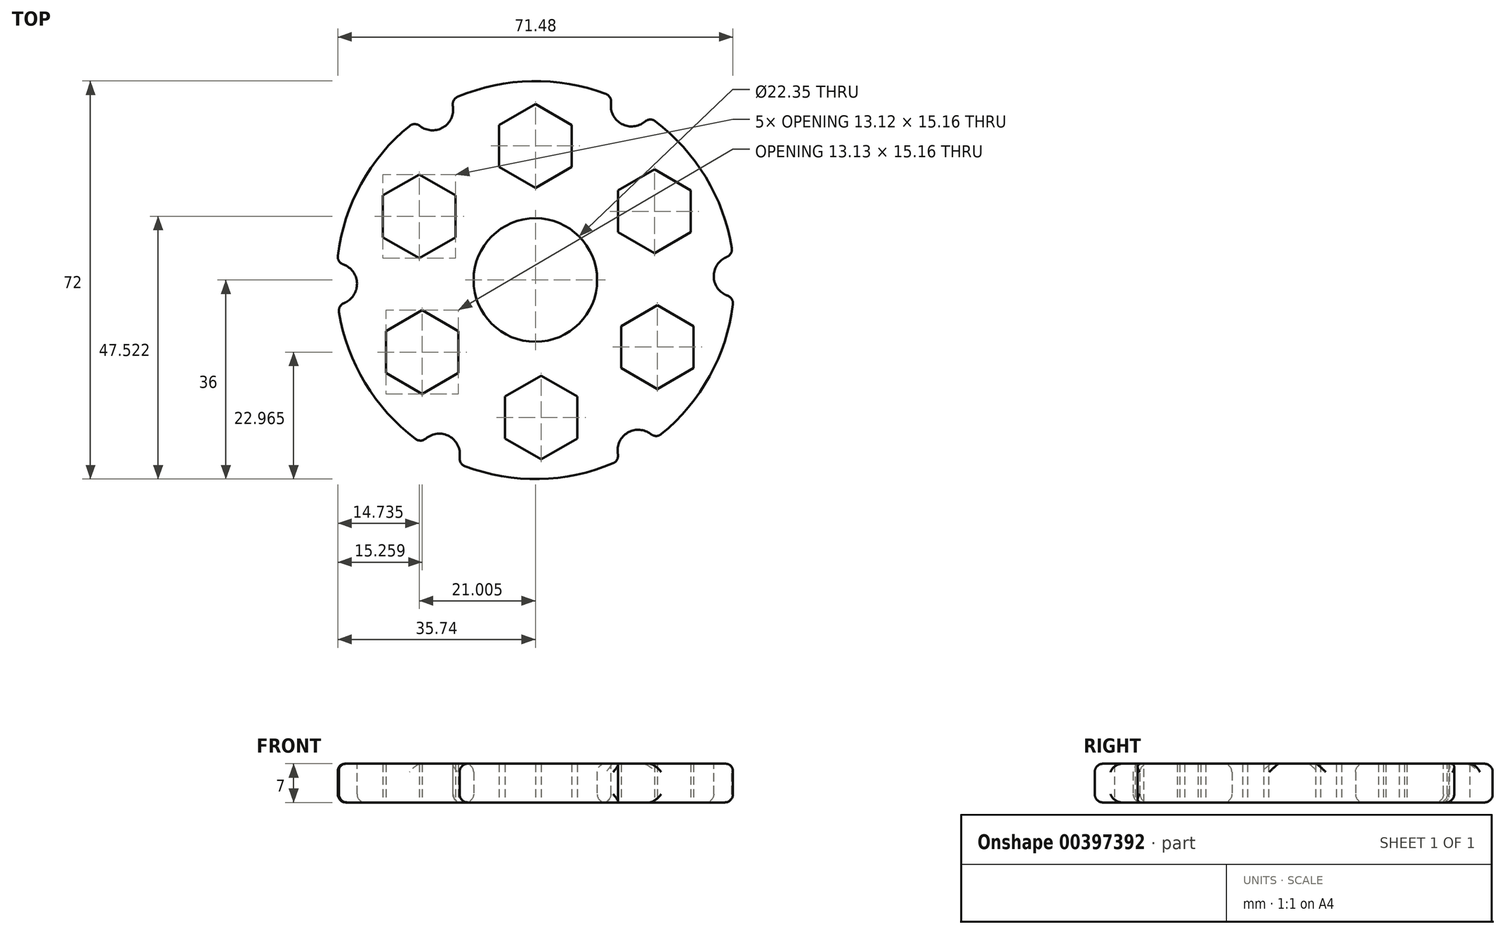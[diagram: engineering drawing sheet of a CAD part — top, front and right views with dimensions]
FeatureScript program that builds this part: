
annotation { "Feature Type Name" : "Feature", "Feature Type Description" : "" }
export const myFeature = defineFeature(function(context is Context, id is Id, definition is map)
    precondition{}
    {
        {
            var Q0;
            Q0=qCreatedBy(makeId("Top.planeOp"),FACE);
            var sketch = newSketch(context, id + "F0", { "sketchPlane" : qUnion([Q0])});
            skCircle(sketch, "E0", {"center": v(0, 0) * mm, "radius": 11.18 * mm});
            skCircle(sketch, "E1", {"center": v(0, 0) * mm, "radius": 36 * mm});
            skCircle(sketch, "E2.cCircle", {"center": v(0, 24.25) * mm, "radius": 6.56 * mm, "construction": true});
            skLineSegment(sketch, "E2.0", {"start": v(6.56, 28.04) * mm, "end": v(6.56, 20.47) * mm});
            skLineSegment(sketch, "E2.1", {"start": v(6.56, 20.47) * mm, "end": v(0, 16.68) * mm});
            skLineSegment(sketch, "E2.2", {"start": v(0, 16.68) * mm, "end": v(-6.56, 20.47) * mm});
            skLineSegment(sketch, "E2.3", {"start": v(-6.56, 20.47) * mm, "end": v(-6.56, 28.04) * mm});
            skLineSegment(sketch, "E2.4", {"start": v(-6.56, 28.04) * mm, "end": v(0, 31.83) * mm});
            skLineSegment(sketch, "E2.5", {"start": v(0, 31.83) * mm, "end": v(6.56, 28.04) * mm});
            skLineSegment(sketch, "E3.1.0", {"start": v(28.1, 8.64) * mm, "end": v(21.53, 4.85) * mm});
            skLineSegment(sketch, "E3.1.1", {"start": v(28.1, 16.22) * mm, "end": v(28.1, 8.64) * mm});
            skLineSegment(sketch, "E3.1.2", {"start": v(21.53, 20) * mm, "end": v(28.1, 16.22) * mm});
            skLineSegment(sketch, "E3.1.3", {"start": v(14.97, 16.22) * mm, "end": v(21.53, 20) * mm});
            skLineSegment(sketch, "E3.1.4", {"start": v(14.97, 8.64) * mm, "end": v(14.97, 16.22) * mm});
            skLineSegment(sketch, "E3.1.5", {"start": v(21.53, 4.85) * mm, "end": v(14.97, 8.64) * mm});
            skLineSegment(sketch, "E3.2.0", {"start": v(22.05, -19.7) * mm, "end": v(15.5, -15.92) * mm});
            skLineSegment(sketch, "E3.2.1", {"start": v(28.62, -15.92) * mm, "end": v(22.05, -19.7) * mm});
            skLineSegment(sketch, "E3.2.2", {"start": v(28.62, -8.34) * mm, "end": v(28.62, -15.92) * mm});
            skLineSegment(sketch, "E3.2.3", {"start": v(22.05, -4.55) * mm, "end": v(28.62, -8.34) * mm});
            skLineSegment(sketch, "E3.2.4", {"start": v(15.5, -8.34) * mm, "end": v(22.05, -4.55) * mm});
            skLineSegment(sketch, "E3.2.5", {"start": v(15.5, -15.92) * mm, "end": v(15.5, -8.34) * mm});
            skLineSegment(sketch, "E3.3.0", {"start": v(-5.51, -28.65) * mm, "end": v(-5.51, -21.07) * mm});
            skLineSegment(sketch, "E3.3.1", {"start": v(1.05, -32.44) * mm, "end": v(-5.51, -28.65) * mm});
            skLineSegment(sketch, "E3.3.2", {"start": v(7.61, -28.65) * mm, "end": v(1.05, -32.44) * mm});
            skLineSegment(sketch, "E3.3.3", {"start": v(7.61, -21.07) * mm, "end": v(7.61, -28.65) * mm});
            skLineSegment(sketch, "E3.3.4", {"start": v(1.05, -17.28) * mm, "end": v(7.61, -21.07) * mm});
            skLineSegment(sketch, "E3.3.5", {"start": v(-5.51, -21.07) * mm, "end": v(1.05, -17.28) * mm});
            skLineSegment(sketch, "E3.4.0", {"start": v(-27.04, -9.25) * mm, "end": v(-20.48, -5.46) * mm});
            skLineSegment(sketch, "E3.4.1", {"start": v(-27.04, -16.82) * mm, "end": v(-27.04, -9.25) * mm});
            skLineSegment(sketch, "E3.4.2", {"start": v(-20.48, -20.61) * mm, "end": v(-27.04, -16.82) * mm});
            skLineSegment(sketch, "E3.4.3", {"start": v(-13.92, -16.82) * mm, "end": v(-20.48, -20.61) * mm});
            skLineSegment(sketch, "E3.4.4", {"start": v(-13.92, -9.25) * mm, "end": v(-13.92, -16.82) * mm});
            skLineSegment(sketch, "E3.4.5", {"start": v(-20.48, -5.46) * mm, "end": v(-13.92, -9.25) * mm});
            skLineSegment(sketch, "E3.5.0", {"start": v(-21, 19.1) * mm, "end": v(-14.44, 15.31) * mm});
            skLineSegment(sketch, "E3.5.1", {"start": v(-27.57, 15.31) * mm, "end": v(-21, 19.1) * mm});
            skLineSegment(sketch, "E3.5.2", {"start": v(-27.57, 7.73) * mm, "end": v(-27.57, 15.31) * mm});
            skLineSegment(sketch, "E3.5.3", {"start": v(-21, 3.94) * mm, "end": v(-27.57, 7.73) * mm});
            skLineSegment(sketch, "E3.5.4", {"start": v(-14.44, 7.73) * mm, "end": v(-21, 3.94) * mm});
            skLineSegment(sketch, "E3.5.5", {"start": v(-14.44, 15.31) * mm, "end": v(-14.44, 7.73) * mm});
            skPoint(sketch, "E3.center", {"position": v(0.52, -0.3) * mm});
            skLineSegment(sketch, "E3.anchor1", {"start": v(0.52, -0.3) * mm, "end": v(6.56, 20.47) * mm, "construction": true});
            skLineSegment(sketch, "E3.anchor2", {"start": v(0.52, -0.3) * mm, "end": v(-14.44, 15.31) * mm, "construction": true});
            skSolve(sketch);
        }
        {
            var Q0;
            Q0=makeQuery(id+"F0.imprint","IMPRINT",FACE,{"disambiguationData":[TD([[makeQuery(id+"F0.imprint","IMPRINT",EDGE,{"derivedFrom":sQuery(id+"F0.wireOp",EDGE,"E0")}),-1.0]])]});
            extrude(context, id + "F1", {"entities" : qUnion([Q0]), "depth" : 7 * mm});
        }
        {
            var Q0;
            Q0=makeQuery(id+"F1.opExtrude","CAP_FACE",FACE,{"disambiguationData":[OSD([sQuery(id+"F0.wireOp",EDGE,"E0"),sQuery(id+"F0.wireOp",EDGE,"E1"),sQuery(id+"F0.wireOp",EDGE,"E2.0"),sQuery(id+"F0.wireOp",EDGE,"E2.1"),sQuery(id+"F0.wireOp",EDGE,"E2.2"),sQuery(id+"F0.wireOp",EDGE,"E2.3"),sQuery(id+"F0.wireOp",EDGE,"E2.4"),sQuery(id+"F0.wireOp",EDGE,"E2.5"),sQuery(id+"F0.wireOp",EDGE,"E3.1.0"),sQuery(id+"F0.wireOp",EDGE,"E3.1.1"),sQuery(id+"F0.wireOp",EDGE,"E3.1.2"),sQuery(id+"F0.wireOp",EDGE,"E3.1.3"),sQuery(id+"F0.wireOp",EDGE,"E3.1.4"),sQuery(id+"F0.wireOp",EDGE,"E3.1.5"),sQuery(id+"F0.wireOp",EDGE,"E3.2.0"),sQuery(id+"F0.wireOp",EDGE,"E3.2.1"),sQuery(id+"F0.wireOp",EDGE,"E3.2.2"),sQuery(id+"F0.wireOp",EDGE,"E3.2.3"),sQuery(id+"F0.wireOp",EDGE,"E3.2.4"),sQuery(id+"F0.wireOp",EDGE,"E3.2.5"),sQuery(id+"F0.wireOp",EDGE,"E3.3.0"),sQuery(id+"F0.wireOp",EDGE,"E3.3.1"),sQuery(id+"F0.wireOp",EDGE,"E3.3.2"),sQuery(id+"F0.wireOp",EDGE,"E3.3.3"),sQuery(id+"F0.wireOp",EDGE,"E3.3.4"),sQuery(id+"F0.wireOp",EDGE,"E3.3.5"),sQuery(id+"F0.wireOp",EDGE,"E3.4.0"),sQuery(id+"F0.wireOp",EDGE,"E3.4.1"),sQuery(id+"F0.wireOp",EDGE,"E3.4.2"),sQuery(id+"F0.wireOp",EDGE,"E3.4.3"),sQuery(id+"F0.wireOp",EDGE,"E3.4.4"),sQuery(id+"F0.wireOp",EDGE,"E3.4.5"),sQuery(id+"F0.wireOp",EDGE,"E3.5.0"),sQuery(id+"F0.wireOp",EDGE,"E3.5.1"),sQuery(id+"F0.wireOp",EDGE,"E3.5.2"),sQuery(id+"F0.wireOp",EDGE,"E3.5.3"),sQuery(id+"F0.wireOp",EDGE,"E3.5.4"),sQuery(id+"F0.wireOp",EDGE,"E3.5.5")])],"isStart":false});
            var sketch = newSketch(context, id + "F2", { "sketchPlane" : qUnion([Q0])});
            skCircle(sketch, "E4", {"center": v(17.4, 31.52) * mm, "radius": 3.73 * mm});
            skCircle(sketch, "E5.1.0", {"center": v(-18.6, 30.82) * mm, "radius": 3.73 * mm});
            skCircle(sketch, "E5.2.0", {"center": v(-36, -0.7) * mm, "radius": 3.73 * mm});
            skCircle(sketch, "E5.3.0", {"center": v(-17.4, -31.52) * mm, "radius": 3.73 * mm});
            skCircle(sketch, "E5.4.0", {"center": v(18.6, -30.82) * mm, "radius": 3.73 * mm});
            skCircle(sketch, "E5.5.0", {"center": v(36, 0.7) * mm, "radius": 3.73 * mm});
            skPoint(sketch, "E5.center", {"position": v(0, 0) * mm});
            skSolve(sketch);
        }
        {
            var Q0;
            {var subQ0=sQuery(id+"F2.wireOp",EDGE,"E5.1.0");var subQ1=makeQuery(id+"F1.opExtrude","CAP_EDGE",EDGE,{"disambiguationData":[OSD([sQuery(id+"F0.wireOp",EDGE,"E1")])],"isStart":false});var subQ2=makeQuery(id+"F2.imprint","INTERSECT",VERTEX,{"disambiguationData":[OD(0.0)],"derivedFrom":[subQ1,subQ0]});Q0=makeQuery(id+"F2.imprint","IMPRINT",FACE,{"disambiguationData":[TD([[makeQuery(id+"F2.imprint","IMPRINT",EDGE,{"disambiguationData":[TD([[subQ2,1.0]])],"derivedFrom":subQ0}),1.0]])]});}
            var Q1;
            {var subQ0=sQuery(id+"F2.wireOp",EDGE,"E5.1.0");var subQ1=makeQuery(id+"F1.opExtrude","CAP_EDGE",EDGE,{"disambiguationData":[OSD([sQuery(id+"F0.wireOp",EDGE,"E1")])],"isStart":false});var subQ2=makeQuery(id+"F2.imprint","INTERSECT",VERTEX,{"disambiguationData":[OD(0.0)],"derivedFrom":[subQ1,subQ0]});Q1=makeQuery(id+"F2.imprint","IMPRINT",FACE,{"disambiguationData":[TD([[makeQuery(id+"F2.imprint","IMPRINT",EDGE,{"disambiguationData":[TD([[subQ2,-1.0]])],"derivedFrom":subQ0}),1.0]])]});}
            var Q2;
            {var subQ0=sQuery(id+"F2.wireOp",EDGE,"E4");var subQ1=makeQuery(id+"F1.opExtrude","CAP_EDGE",EDGE,{"disambiguationData":[OSD([sQuery(id+"F0.wireOp",EDGE,"E1")])],"isStart":false});var subQ2=makeQuery(id+"F2.imprint","INTERSECT",VERTEX,{"disambiguationData":[OD(0.0)],"derivedFrom":[subQ1,subQ0]});Q2=makeQuery(id+"F2.imprint","IMPRINT",FACE,{"disambiguationData":[TD([[makeQuery(id+"F2.imprint","IMPRINT",EDGE,{"disambiguationData":[TD([[subQ2,1.0]])],"derivedFrom":subQ0}),1.0]])]});}
            var Q3;
            {var subQ0=sQuery(id+"F2.wireOp",EDGE,"E4");var subQ1=makeQuery(id+"F1.opExtrude","CAP_EDGE",EDGE,{"disambiguationData":[OSD([sQuery(id+"F0.wireOp",EDGE,"E1")])],"isStart":false});var subQ2=makeQuery(id+"F2.imprint","INTERSECT",VERTEX,{"disambiguationData":[OD(0.0)],"derivedFrom":[subQ1,subQ0]});Q3=makeQuery(id+"F2.imprint","IMPRINT",FACE,{"disambiguationData":[TD([[makeQuery(id+"F2.imprint","IMPRINT",EDGE,{"disambiguationData":[TD([[subQ2,-1.0]])],"derivedFrom":subQ0}),1.0]])]});}
            var Q4;
            {var subQ0=sQuery(id+"F2.wireOp",EDGE,"E5.5.0");var subQ1=makeQuery(id+"F1.opExtrude","CAP_EDGE",EDGE,{"disambiguationData":[OSD([sQuery(id+"F0.wireOp",EDGE,"E1")])],"isStart":false});var subQ2=makeQuery(id+"F2.imprint","INTERSECT",VERTEX,{"disambiguationData":[OD(0.0)],"derivedFrom":[subQ1,subQ0]});Q4=makeQuery(id+"F2.imprint","IMPRINT",FACE,{"disambiguationData":[TD([[makeQuery(id+"F2.imprint","IMPRINT",EDGE,{"disambiguationData":[TD([[subQ2,-1.0]])],"derivedFrom":subQ0}),1.0]])]});}
            var Q5;
            {var subQ0=sQuery(id+"F2.wireOp",EDGE,"E5.5.0");var subQ1=makeQuery(id+"F1.opExtrude","CAP_EDGE",EDGE,{"disambiguationData":[OSD([sQuery(id+"F0.wireOp",EDGE,"E1")])],"isStart":false});var subQ2=makeQuery(id+"F2.imprint","INTERSECT",VERTEX,{"disambiguationData":[OD(0.0)],"derivedFrom":[subQ1,subQ0]});Q5=makeQuery(id+"F2.imprint","IMPRINT",FACE,{"disambiguationData":[TD([[makeQuery(id+"F2.imprint","IMPRINT",EDGE,{"disambiguationData":[TD([[subQ2,1.0]])],"derivedFrom":subQ0}),1.0]])]});}
            var Q6;
            {var subQ0=sQuery(id+"F2.wireOp",EDGE,"E5.4.0");var subQ1=makeQuery(id+"F1.opExtrude","CAP_EDGE",EDGE,{"disambiguationData":[OSD([sQuery(id+"F0.wireOp",EDGE,"E1")])],"isStart":false});var subQ2=makeQuery(id+"F2.imprint","INTERSECT",VERTEX,{"disambiguationData":[OD(0.0)],"derivedFrom":[subQ1,subQ0]});Q6=makeQuery(id+"F2.imprint","IMPRINT",FACE,{"disambiguationData":[TD([[makeQuery(id+"F2.imprint","IMPRINT",EDGE,{"disambiguationData":[TD([[subQ2,-1.0]])],"derivedFrom":subQ0}),1.0]])]});}
            var Q7;
            {var subQ0=sQuery(id+"F2.wireOp",EDGE,"E5.4.0");var subQ1=makeQuery(id+"F1.opExtrude","CAP_EDGE",EDGE,{"disambiguationData":[OSD([sQuery(id+"F0.wireOp",EDGE,"E1")])],"isStart":false});var subQ2=makeQuery(id+"F2.imprint","INTERSECT",VERTEX,{"disambiguationData":[OD(0.0)],"derivedFrom":[subQ1,subQ0]});Q7=makeQuery(id+"F2.imprint","IMPRINT",FACE,{"disambiguationData":[TD([[makeQuery(id+"F2.imprint","IMPRINT",EDGE,{"disambiguationData":[TD([[subQ2,1.0]])],"derivedFrom":subQ0}),1.0]])]});}
            var Q8;
            {var subQ0=sQuery(id+"F2.wireOp",EDGE,"E5.3.0");var subQ1=makeQuery(id+"F1.opExtrude","CAP_EDGE",EDGE,{"disambiguationData":[OSD([sQuery(id+"F0.wireOp",EDGE,"E1")])],"isStart":false});var subQ2=makeQuery(id+"F2.imprint","INTERSECT",VERTEX,{"disambiguationData":[OD(0.0)],"derivedFrom":[subQ1,subQ0]});Q8=makeQuery(id+"F2.imprint","IMPRINT",FACE,{"disambiguationData":[TD([[makeQuery(id+"F2.imprint","IMPRINT",EDGE,{"disambiguationData":[TD([[subQ2,-1.0]])],"derivedFrom":subQ0}),1.0]])]});}
            var Q9;
            {var subQ0=sQuery(id+"F2.wireOp",EDGE,"E5.3.0");var subQ1=makeQuery(id+"F1.opExtrude","CAP_EDGE",EDGE,{"disambiguationData":[OSD([sQuery(id+"F0.wireOp",EDGE,"E1")])],"isStart":false});var subQ2=makeQuery(id+"F2.imprint","INTERSECT",VERTEX,{"disambiguationData":[OD(0.0)],"derivedFrom":[subQ1,subQ0]});Q9=makeQuery(id+"F2.imprint","IMPRINT",FACE,{"disambiguationData":[TD([[makeQuery(id+"F2.imprint","IMPRINT",EDGE,{"disambiguationData":[TD([[subQ2,1.0]])],"derivedFrom":subQ0}),1.0]])]});}
            var Q10;
            {var subQ0=sQuery(id+"F2.wireOp",EDGE,"E5.2.0");var subQ1=makeQuery(id+"F1.opExtrude","CAP_EDGE",EDGE,{"disambiguationData":[OSD([sQuery(id+"F0.wireOp",EDGE,"E1")])],"isStart":false});var subQ2=makeQuery(id+"F2.imprint","INTERSECT",VERTEX,{"disambiguationData":[OD(0.0)],"derivedFrom":[subQ1,subQ0]});Q10=makeQuery(id+"F2.imprint","IMPRINT",FACE,{"disambiguationData":[TD([[makeQuery(id+"F2.imprint","IMPRINT",EDGE,{"disambiguationData":[TD([[subQ2,1.0]])],"derivedFrom":subQ0}),1.0]])]});}
            var Q11;
            {var subQ0=sQuery(id+"F2.wireOp",EDGE,"E5.2.0");var subQ1=makeQuery(id+"F1.opExtrude","CAP_EDGE",EDGE,{"disambiguationData":[OSD([sQuery(id+"F0.wireOp",EDGE,"E1")])],"isStart":false});var subQ2=makeQuery(id+"F2.imprint","INTERSECT",VERTEX,{"disambiguationData":[OD(0.0)],"derivedFrom":[subQ1,subQ0]});Q11=makeQuery(id+"F2.imprint","IMPRINT",FACE,{"disambiguationData":[TD([[makeQuery(id+"F2.imprint","IMPRINT",EDGE,{"disambiguationData":[TD([[subQ2,-1.0]])],"derivedFrom":subQ0}),1.0]])]});}
            extrude(context, id + "F3", {"entities" : qUnion([Q0, Q1, Q2, Q3, Q4, Q5, Q6, Q7, Q8, Q9, Q10, Q11]), "operationType" : NewBodyOperationType.REMOVE, "oppositeDirection" : true, "depth" : 25 * mm});
        }
        {
            var Q0;
            {var subQ0=sQuery(id+"F0.wireOp",EDGE,"E1");Q0=makeQuery(id+"F3.boolean.opBoolean","SPLIT",EDGE,{"disambiguationData":[TD([makeQuery(id+"F1.opExtrude","CAP_FACE",FACE,{"disambiguationData":[OSD([sQuery(id+"F0.wireOp",EDGE,"E0"),subQ0,sQuery(id+"F0.wireOp",EDGE,"E2.0"),sQuery(id+"F0.wireOp",EDGE,"E2.1"),sQuery(id+"F0.wireOp",EDGE,"E2.2"),sQuery(id+"F0.wireOp",EDGE,"E2.3"),sQuery(id+"F0.wireOp",EDGE,"E2.4"),sQuery(id+"F0.wireOp",EDGE,"E2.5"),sQuery(id+"F0.wireOp",EDGE,"E3.1.0"),sQuery(id+"F0.wireOp",EDGE,"E3.1.1"),sQuery(id+"F0.wireOp",EDGE,"E3.1.2"),sQuery(id+"F0.wireOp",EDGE,"E3.1.3"),sQuery(id+"F0.wireOp",EDGE,"E3.1.4"),sQuery(id+"F0.wireOp",EDGE,"E3.1.5"),sQuery(id+"F0.wireOp",EDGE,"E3.2.0"),sQuery(id+"F0.wireOp",EDGE,"E3.2.1"),sQuery(id+"F0.wireOp",EDGE,"E3.2.2"),sQuery(id+"F0.wireOp",EDGE,"E3.2.3"),sQuery(id+"F0.wireOp",EDGE,"E3.2.4"),sQuery(id+"F0.wireOp",EDGE,"E3.2.5"),sQuery(id+"F0.wireOp",EDGE,"E3.3.0"),sQuery(id+"F0.wireOp",EDGE,"E3.3.1"),sQuery(id+"F0.wireOp",EDGE,"E3.3.2"),sQuery(id+"F0.wireOp",EDGE,"E3.3.3"),sQuery(id+"F0.wireOp",EDGE,"E3.3.4"),sQuery(id+"F0.wireOp",EDGE,"E3.3.5"),sQuery(id+"F0.wireOp",EDGE,"E3.4.0"),sQuery(id+"F0.wireOp",EDGE,"E3.4.1"),sQuery(id+"F0.wireOp",EDGE,"E3.4.2"),sQuery(id+"F0.wireOp",EDGE,"E3.4.3"),sQuery(id+"F0.wireOp",EDGE,"E3.4.4"),sQuery(id+"F0.wireOp",EDGE,"E3.4.5"),sQuery(id+"F0.wireOp",EDGE,"E3.5.0"),sQuery(id+"F0.wireOp",EDGE,"E3.5.1"),sQuery(id+"F0.wireOp",EDGE,"E3.5.2"),sQuery(id+"F0.wireOp",EDGE,"E3.5.3"),sQuery(id+"F0.wireOp",EDGE,"E3.5.4"),sQuery(id+"F0.wireOp",EDGE,"E3.5.5")])],"isStart":false}),makeQuery(id+"F1.opExtrude","SWEPT_FACE",FACE,{"disambiguationData":[OSD([subQ0])]}),makeQuery(id+"F3.opExtrude","SWEPT_FACE",FACE,{"disambiguationData":[OSD([sQuery(id+"F2.wireOp",EDGE,"E5.1.0")])]}),makeQuery(id+"F3.opExtrude","SWEPT_FACE",FACE,{"disambiguationData":[OSD([sQuery(id+"F2.wireOp",EDGE,"E5.2.0")])]})])],"derivedFrom":makeQuery(id+"F1.opExtrude","CAP_EDGE",EDGE,{"disambiguationData":[OSD([subQ0])],"isStart":false})});}
            var Q1;
            Q1=makeQuery(id+"F3.boolean.opBoolean","COPY",EDGE,{"derivedFrom":makeQuery(id+"F3.opExtrude","CAP_EDGE",EDGE,{"disambiguationData":[OSD([sQuery(id+"F2.wireOp",EDGE,"E5.1.0")])],"isStart":true})});
            var Q2;
            {var subQ0=sQuery(id+"F0.wireOp",EDGE,"E1");Q2=makeQuery(id+"F3.boolean.opBoolean","SPLIT",EDGE,{"disambiguationData":[TD([makeQuery(id+"F1.opExtrude","CAP_FACE",FACE,{"disambiguationData":[OSD([sQuery(id+"F0.wireOp",EDGE,"E0"),subQ0,sQuery(id+"F0.wireOp",EDGE,"E2.0"),sQuery(id+"F0.wireOp",EDGE,"E2.1"),sQuery(id+"F0.wireOp",EDGE,"E2.2"),sQuery(id+"F0.wireOp",EDGE,"E2.3"),sQuery(id+"F0.wireOp",EDGE,"E2.4"),sQuery(id+"F0.wireOp",EDGE,"E2.5"),sQuery(id+"F0.wireOp",EDGE,"E3.1.0"),sQuery(id+"F0.wireOp",EDGE,"E3.1.1"),sQuery(id+"F0.wireOp",EDGE,"E3.1.2"),sQuery(id+"F0.wireOp",EDGE,"E3.1.3"),sQuery(id+"F0.wireOp",EDGE,"E3.1.4"),sQuery(id+"F0.wireOp",EDGE,"E3.1.5"),sQuery(id+"F0.wireOp",EDGE,"E3.2.0"),sQuery(id+"F0.wireOp",EDGE,"E3.2.1"),sQuery(id+"F0.wireOp",EDGE,"E3.2.2"),sQuery(id+"F0.wireOp",EDGE,"E3.2.3"),sQuery(id+"F0.wireOp",EDGE,"E3.2.4"),sQuery(id+"F0.wireOp",EDGE,"E3.2.5"),sQuery(id+"F0.wireOp",EDGE,"E3.3.0"),sQuery(id+"F0.wireOp",EDGE,"E3.3.1"),sQuery(id+"F0.wireOp",EDGE,"E3.3.2"),sQuery(id+"F0.wireOp",EDGE,"E3.3.3"),sQuery(id+"F0.wireOp",EDGE,"E3.3.4"),sQuery(id+"F0.wireOp",EDGE,"E3.3.5"),sQuery(id+"F0.wireOp",EDGE,"E3.4.0"),sQuery(id+"F0.wireOp",EDGE,"E3.4.1"),sQuery(id+"F0.wireOp",EDGE,"E3.4.2"),sQuery(id+"F0.wireOp",EDGE,"E3.4.3"),sQuery(id+"F0.wireOp",EDGE,"E3.4.4"),sQuery(id+"F0.wireOp",EDGE,"E3.4.5"),sQuery(id+"F0.wireOp",EDGE,"E3.5.0"),sQuery(id+"F0.wireOp",EDGE,"E3.5.1"),sQuery(id+"F0.wireOp",EDGE,"E3.5.2"),sQuery(id+"F0.wireOp",EDGE,"E3.5.3"),sQuery(id+"F0.wireOp",EDGE,"E3.5.4"),sQuery(id+"F0.wireOp",EDGE,"E3.5.5")])],"isStart":false}),makeQuery(id+"F1.opExtrude","SWEPT_FACE",FACE,{"disambiguationData":[OSD([subQ0])]}),makeQuery(id+"F3.opExtrude","SWEPT_FACE",FACE,{"disambiguationData":[OSD([sQuery(id+"F2.wireOp",EDGE,"E4")])]}),makeQuery(id+"F3.opExtrude","SWEPT_FACE",FACE,{"disambiguationData":[OSD([sQuery(id+"F2.wireOp",EDGE,"E5.1.0")])]})])],"derivedFrom":makeQuery(id+"F1.opExtrude","CAP_EDGE",EDGE,{"disambiguationData":[OSD([subQ0])],"isStart":false})});}
            var Q3;
            Q3=makeQuery(id+"F3.boolean.opBoolean","COPY",EDGE,{"derivedFrom":makeQuery(id+"F3.opExtrude","CAP_EDGE",EDGE,{"disambiguationData":[OSD([sQuery(id+"F2.wireOp",EDGE,"E4")])],"isStart":true})});
            var Q4;
            {var subQ0=sQuery(id+"F0.wireOp",EDGE,"E1");Q4=makeQuery(id+"F3.boolean.opBoolean","SPLIT",EDGE,{"disambiguationData":[TD([makeQuery(id+"F1.opExtrude","CAP_FACE",FACE,{"disambiguationData":[OSD([sQuery(id+"F0.wireOp",EDGE,"E0"),subQ0,sQuery(id+"F0.wireOp",EDGE,"E2.0"),sQuery(id+"F0.wireOp",EDGE,"E2.1"),sQuery(id+"F0.wireOp",EDGE,"E2.2"),sQuery(id+"F0.wireOp",EDGE,"E2.3"),sQuery(id+"F0.wireOp",EDGE,"E2.4"),sQuery(id+"F0.wireOp",EDGE,"E2.5"),sQuery(id+"F0.wireOp",EDGE,"E3.1.0"),sQuery(id+"F0.wireOp",EDGE,"E3.1.1"),sQuery(id+"F0.wireOp",EDGE,"E3.1.2"),sQuery(id+"F0.wireOp",EDGE,"E3.1.3"),sQuery(id+"F0.wireOp",EDGE,"E3.1.4"),sQuery(id+"F0.wireOp",EDGE,"E3.1.5"),sQuery(id+"F0.wireOp",EDGE,"E3.2.0"),sQuery(id+"F0.wireOp",EDGE,"E3.2.1"),sQuery(id+"F0.wireOp",EDGE,"E3.2.2"),sQuery(id+"F0.wireOp",EDGE,"E3.2.3"),sQuery(id+"F0.wireOp",EDGE,"E3.2.4"),sQuery(id+"F0.wireOp",EDGE,"E3.2.5"),sQuery(id+"F0.wireOp",EDGE,"E3.3.0"),sQuery(id+"F0.wireOp",EDGE,"E3.3.1"),sQuery(id+"F0.wireOp",EDGE,"E3.3.2"),sQuery(id+"F0.wireOp",EDGE,"E3.3.3"),sQuery(id+"F0.wireOp",EDGE,"E3.3.4"),sQuery(id+"F0.wireOp",EDGE,"E3.3.5"),sQuery(id+"F0.wireOp",EDGE,"E3.4.0"),sQuery(id+"F0.wireOp",EDGE,"E3.4.1"),sQuery(id+"F0.wireOp",EDGE,"E3.4.2"),sQuery(id+"F0.wireOp",EDGE,"E3.4.3"),sQuery(id+"F0.wireOp",EDGE,"E3.4.4"),sQuery(id+"F0.wireOp",EDGE,"E3.4.5"),sQuery(id+"F0.wireOp",EDGE,"E3.5.0"),sQuery(id+"F0.wireOp",EDGE,"E3.5.1"),sQuery(id+"F0.wireOp",EDGE,"E3.5.2"),sQuery(id+"F0.wireOp",EDGE,"E3.5.3"),sQuery(id+"F0.wireOp",EDGE,"E3.5.4"),sQuery(id+"F0.wireOp",EDGE,"E3.5.5")])],"isStart":false}),makeQuery(id+"F1.opExtrude","SWEPT_FACE",FACE,{"disambiguationData":[OSD([subQ0])]}),makeQuery(id+"F3.opExtrude","SWEPT_FACE",FACE,{"disambiguationData":[OSD([sQuery(id+"F2.wireOp",EDGE,"E4")])]}),makeQuery(id+"F3.opExtrude","SWEPT_FACE",FACE,{"disambiguationData":[OSD([sQuery(id+"F2.wireOp",EDGE,"E5.5.0")])]})])],"derivedFrom":makeQuery(id+"F1.opExtrude","CAP_EDGE",EDGE,{"disambiguationData":[OSD([subQ0])],"isStart":false})});}
            var Q5;
            Q5=makeQuery(id+"F3.boolean.opBoolean","COPY",EDGE,{"derivedFrom":makeQuery(id+"F3.opExtrude","CAP_EDGE",EDGE,{"disambiguationData":[OSD([sQuery(id+"F2.wireOp",EDGE,"E5.5.0")])],"isStart":true})});
            var Q6;
            {var subQ0=sQuery(id+"F0.wireOp",EDGE,"E1");Q6=makeQuery(id+"F3.boolean.opBoolean","SPLIT",EDGE,{"disambiguationData":[TD([makeQuery(id+"F1.opExtrude","CAP_FACE",FACE,{"disambiguationData":[OSD([sQuery(id+"F0.wireOp",EDGE,"E0"),subQ0,sQuery(id+"F0.wireOp",EDGE,"E2.0"),sQuery(id+"F0.wireOp",EDGE,"E2.1"),sQuery(id+"F0.wireOp",EDGE,"E2.2"),sQuery(id+"F0.wireOp",EDGE,"E2.3"),sQuery(id+"F0.wireOp",EDGE,"E2.4"),sQuery(id+"F0.wireOp",EDGE,"E2.5"),sQuery(id+"F0.wireOp",EDGE,"E3.1.0"),sQuery(id+"F0.wireOp",EDGE,"E3.1.1"),sQuery(id+"F0.wireOp",EDGE,"E3.1.2"),sQuery(id+"F0.wireOp",EDGE,"E3.1.3"),sQuery(id+"F0.wireOp",EDGE,"E3.1.4"),sQuery(id+"F0.wireOp",EDGE,"E3.1.5"),sQuery(id+"F0.wireOp",EDGE,"E3.2.0"),sQuery(id+"F0.wireOp",EDGE,"E3.2.1"),sQuery(id+"F0.wireOp",EDGE,"E3.2.2"),sQuery(id+"F0.wireOp",EDGE,"E3.2.3"),sQuery(id+"F0.wireOp",EDGE,"E3.2.4"),sQuery(id+"F0.wireOp",EDGE,"E3.2.5"),sQuery(id+"F0.wireOp",EDGE,"E3.3.0"),sQuery(id+"F0.wireOp",EDGE,"E3.3.1"),sQuery(id+"F0.wireOp",EDGE,"E3.3.2"),sQuery(id+"F0.wireOp",EDGE,"E3.3.3"),sQuery(id+"F0.wireOp",EDGE,"E3.3.4"),sQuery(id+"F0.wireOp",EDGE,"E3.3.5"),sQuery(id+"F0.wireOp",EDGE,"E3.4.0"),sQuery(id+"F0.wireOp",EDGE,"E3.4.1"),sQuery(id+"F0.wireOp",EDGE,"E3.4.2"),sQuery(id+"F0.wireOp",EDGE,"E3.4.3"),sQuery(id+"F0.wireOp",EDGE,"E3.4.4"),sQuery(id+"F0.wireOp",EDGE,"E3.4.5"),sQuery(id+"F0.wireOp",EDGE,"E3.5.0"),sQuery(id+"F0.wireOp",EDGE,"E3.5.1"),sQuery(id+"F0.wireOp",EDGE,"E3.5.2"),sQuery(id+"F0.wireOp",EDGE,"E3.5.3"),sQuery(id+"F0.wireOp",EDGE,"E3.5.4"),sQuery(id+"F0.wireOp",EDGE,"E3.5.5")])],"isStart":false}),makeQuery(id+"F1.opExtrude","SWEPT_FACE",FACE,{"disambiguationData":[OSD([subQ0])]}),makeQuery(id+"F3.opExtrude","SWEPT_FACE",FACE,{"disambiguationData":[OSD([sQuery(id+"F2.wireOp",EDGE,"E5.4.0")])]}),makeQuery(id+"F3.opExtrude","SWEPT_FACE",FACE,{"disambiguationData":[OSD([sQuery(id+"F2.wireOp",EDGE,"E5.5.0")])]})])],"derivedFrom":makeQuery(id+"F1.opExtrude","CAP_EDGE",EDGE,{"disambiguationData":[OSD([subQ0])],"isStart":false})});}
            var Q7;
            Q7=makeQuery(id+"F3.boolean.opBoolean","COPY",EDGE,{"derivedFrom":makeQuery(id+"F3.opExtrude","CAP_EDGE",EDGE,{"disambiguationData":[OSD([sQuery(id+"F2.wireOp",EDGE,"E5.4.0")])],"isStart":true})});
            var Q8;
            {var subQ0=sQuery(id+"F0.wireOp",EDGE,"E1");Q8=makeQuery(id+"F3.boolean.opBoolean","SPLIT",EDGE,{"disambiguationData":[TD([makeQuery(id+"F1.opExtrude","CAP_FACE",FACE,{"disambiguationData":[OSD([sQuery(id+"F0.wireOp",EDGE,"E0"),subQ0,sQuery(id+"F0.wireOp",EDGE,"E2.0"),sQuery(id+"F0.wireOp",EDGE,"E2.1"),sQuery(id+"F0.wireOp",EDGE,"E2.2"),sQuery(id+"F0.wireOp",EDGE,"E2.3"),sQuery(id+"F0.wireOp",EDGE,"E2.4"),sQuery(id+"F0.wireOp",EDGE,"E2.5"),sQuery(id+"F0.wireOp",EDGE,"E3.1.0"),sQuery(id+"F0.wireOp",EDGE,"E3.1.1"),sQuery(id+"F0.wireOp",EDGE,"E3.1.2"),sQuery(id+"F0.wireOp",EDGE,"E3.1.3"),sQuery(id+"F0.wireOp",EDGE,"E3.1.4"),sQuery(id+"F0.wireOp",EDGE,"E3.1.5"),sQuery(id+"F0.wireOp",EDGE,"E3.2.0"),sQuery(id+"F0.wireOp",EDGE,"E3.2.1"),sQuery(id+"F0.wireOp",EDGE,"E3.2.2"),sQuery(id+"F0.wireOp",EDGE,"E3.2.3"),sQuery(id+"F0.wireOp",EDGE,"E3.2.4"),sQuery(id+"F0.wireOp",EDGE,"E3.2.5"),sQuery(id+"F0.wireOp",EDGE,"E3.3.0"),sQuery(id+"F0.wireOp",EDGE,"E3.3.1"),sQuery(id+"F0.wireOp",EDGE,"E3.3.2"),sQuery(id+"F0.wireOp",EDGE,"E3.3.3"),sQuery(id+"F0.wireOp",EDGE,"E3.3.4"),sQuery(id+"F0.wireOp",EDGE,"E3.3.5"),sQuery(id+"F0.wireOp",EDGE,"E3.4.0"),sQuery(id+"F0.wireOp",EDGE,"E3.4.1"),sQuery(id+"F0.wireOp",EDGE,"E3.4.2"),sQuery(id+"F0.wireOp",EDGE,"E3.4.3"),sQuery(id+"F0.wireOp",EDGE,"E3.4.4"),sQuery(id+"F0.wireOp",EDGE,"E3.4.5"),sQuery(id+"F0.wireOp",EDGE,"E3.5.0"),sQuery(id+"F0.wireOp",EDGE,"E3.5.1"),sQuery(id+"F0.wireOp",EDGE,"E3.5.2"),sQuery(id+"F0.wireOp",EDGE,"E3.5.3"),sQuery(id+"F0.wireOp",EDGE,"E3.5.4"),sQuery(id+"F0.wireOp",EDGE,"E3.5.5")])],"isStart":false}),makeQuery(id+"F1.opExtrude","SWEPT_FACE",FACE,{"disambiguationData":[OSD([subQ0])]}),makeQuery(id+"F3.opExtrude","SWEPT_FACE",FACE,{"disambiguationData":[OSD([sQuery(id+"F2.wireOp",EDGE,"E5.3.0")])]}),makeQuery(id+"F3.opExtrude","SWEPT_FACE",FACE,{"disambiguationData":[OSD([sQuery(id+"F2.wireOp",EDGE,"E5.4.0")])]})])],"derivedFrom":makeQuery(id+"F1.opExtrude","CAP_EDGE",EDGE,{"disambiguationData":[OSD([subQ0])],"isStart":false})});}
            var Q9;
            Q9=makeQuery(id+"F3.boolean.opBoolean","COPY",EDGE,{"derivedFrom":makeQuery(id+"F3.opExtrude","CAP_EDGE",EDGE,{"disambiguationData":[OSD([sQuery(id+"F2.wireOp",EDGE,"E5.3.0")])],"isStart":true})});
            var Q10;
            {var subQ0=sQuery(id+"F0.wireOp",EDGE,"E1");Q10=makeQuery(id+"F3.boolean.opBoolean","SPLIT",EDGE,{"disambiguationData":[TD([makeQuery(id+"F1.opExtrude","CAP_FACE",FACE,{"disambiguationData":[OSD([sQuery(id+"F0.wireOp",EDGE,"E0"),subQ0,sQuery(id+"F0.wireOp",EDGE,"E2.0"),sQuery(id+"F0.wireOp",EDGE,"E2.1"),sQuery(id+"F0.wireOp",EDGE,"E2.2"),sQuery(id+"F0.wireOp",EDGE,"E2.3"),sQuery(id+"F0.wireOp",EDGE,"E2.4"),sQuery(id+"F0.wireOp",EDGE,"E2.5"),sQuery(id+"F0.wireOp",EDGE,"E3.1.0"),sQuery(id+"F0.wireOp",EDGE,"E3.1.1"),sQuery(id+"F0.wireOp",EDGE,"E3.1.2"),sQuery(id+"F0.wireOp",EDGE,"E3.1.3"),sQuery(id+"F0.wireOp",EDGE,"E3.1.4"),sQuery(id+"F0.wireOp",EDGE,"E3.1.5"),sQuery(id+"F0.wireOp",EDGE,"E3.2.0"),sQuery(id+"F0.wireOp",EDGE,"E3.2.1"),sQuery(id+"F0.wireOp",EDGE,"E3.2.2"),sQuery(id+"F0.wireOp",EDGE,"E3.2.3"),sQuery(id+"F0.wireOp",EDGE,"E3.2.4"),sQuery(id+"F0.wireOp",EDGE,"E3.2.5"),sQuery(id+"F0.wireOp",EDGE,"E3.3.0"),sQuery(id+"F0.wireOp",EDGE,"E3.3.1"),sQuery(id+"F0.wireOp",EDGE,"E3.3.2"),sQuery(id+"F0.wireOp",EDGE,"E3.3.3"),sQuery(id+"F0.wireOp",EDGE,"E3.3.4"),sQuery(id+"F0.wireOp",EDGE,"E3.3.5"),sQuery(id+"F0.wireOp",EDGE,"E3.4.0"),sQuery(id+"F0.wireOp",EDGE,"E3.4.1"),sQuery(id+"F0.wireOp",EDGE,"E3.4.2"),sQuery(id+"F0.wireOp",EDGE,"E3.4.3"),sQuery(id+"F0.wireOp",EDGE,"E3.4.4"),sQuery(id+"F0.wireOp",EDGE,"E3.4.5"),sQuery(id+"F0.wireOp",EDGE,"E3.5.0"),sQuery(id+"F0.wireOp",EDGE,"E3.5.1"),sQuery(id+"F0.wireOp",EDGE,"E3.5.2"),sQuery(id+"F0.wireOp",EDGE,"E3.5.3"),sQuery(id+"F0.wireOp",EDGE,"E3.5.4"),sQuery(id+"F0.wireOp",EDGE,"E3.5.5")])],"isStart":false}),makeQuery(id+"F1.opExtrude","SWEPT_FACE",FACE,{"disambiguationData":[OSD([subQ0])]}),makeQuery(id+"F3.opExtrude","SWEPT_FACE",FACE,{"disambiguationData":[OSD([sQuery(id+"F2.wireOp",EDGE,"E5.2.0")])]}),makeQuery(id+"F3.opExtrude","SWEPT_FACE",FACE,{"disambiguationData":[OSD([sQuery(id+"F2.wireOp",EDGE,"E5.3.0")])]})])],"derivedFrom":makeQuery(id+"F1.opExtrude","CAP_EDGE",EDGE,{"disambiguationData":[OSD([subQ0])],"isStart":false})});}
            var Q11;
            Q11=makeQuery(id+"F3.boolean.opBoolean","COPY",EDGE,{"derivedFrom":makeQuery(id+"F3.opExtrude","CAP_EDGE",EDGE,{"disambiguationData":[OSD([sQuery(id+"F2.wireOp",EDGE,"E5.2.0")])],"isStart":true})});
            var Q12;
            {var subQ0=sQuery(id+"F0.wireOp",EDGE,"E1");Q12=makeQuery(id+"F3.boolean.opBoolean","SPLIT",EDGE,{"disambiguationData":[TD([makeQuery(id+"F1.opExtrude","CAP_FACE",FACE,{"disambiguationData":[OSD([sQuery(id+"F0.wireOp",EDGE,"E0"),subQ0,sQuery(id+"F0.wireOp",EDGE,"E2.0"),sQuery(id+"F0.wireOp",EDGE,"E2.1"),sQuery(id+"F0.wireOp",EDGE,"E2.2"),sQuery(id+"F0.wireOp",EDGE,"E2.3"),sQuery(id+"F0.wireOp",EDGE,"E2.4"),sQuery(id+"F0.wireOp",EDGE,"E2.5"),sQuery(id+"F0.wireOp",EDGE,"E3.1.0"),sQuery(id+"F0.wireOp",EDGE,"E3.1.1"),sQuery(id+"F0.wireOp",EDGE,"E3.1.2"),sQuery(id+"F0.wireOp",EDGE,"E3.1.3"),sQuery(id+"F0.wireOp",EDGE,"E3.1.4"),sQuery(id+"F0.wireOp",EDGE,"E3.1.5"),sQuery(id+"F0.wireOp",EDGE,"E3.2.0"),sQuery(id+"F0.wireOp",EDGE,"E3.2.1"),sQuery(id+"F0.wireOp",EDGE,"E3.2.2"),sQuery(id+"F0.wireOp",EDGE,"E3.2.3"),sQuery(id+"F0.wireOp",EDGE,"E3.2.4"),sQuery(id+"F0.wireOp",EDGE,"E3.2.5"),sQuery(id+"F0.wireOp",EDGE,"E3.3.0"),sQuery(id+"F0.wireOp",EDGE,"E3.3.1"),sQuery(id+"F0.wireOp",EDGE,"E3.3.2"),sQuery(id+"F0.wireOp",EDGE,"E3.3.3"),sQuery(id+"F0.wireOp",EDGE,"E3.3.4"),sQuery(id+"F0.wireOp",EDGE,"E3.3.5"),sQuery(id+"F0.wireOp",EDGE,"E3.4.0"),sQuery(id+"F0.wireOp",EDGE,"E3.4.1"),sQuery(id+"F0.wireOp",EDGE,"E3.4.2"),sQuery(id+"F0.wireOp",EDGE,"E3.4.3"),sQuery(id+"F0.wireOp",EDGE,"E3.4.4"),sQuery(id+"F0.wireOp",EDGE,"E3.4.5"),sQuery(id+"F0.wireOp",EDGE,"E3.5.0"),sQuery(id+"F0.wireOp",EDGE,"E3.5.1"),sQuery(id+"F0.wireOp",EDGE,"E3.5.2"),sQuery(id+"F0.wireOp",EDGE,"E3.5.3"),sQuery(id+"F0.wireOp",EDGE,"E3.5.4"),sQuery(id+"F0.wireOp",EDGE,"E3.5.5")])],"isStart":true}),makeQuery(id+"F1.opExtrude","SWEPT_FACE",FACE,{"disambiguationData":[OSD([subQ0])]}),makeQuery(id+"F3.opExtrude","SWEPT_FACE",FACE,{"disambiguationData":[OSD([sQuery(id+"F2.wireOp",EDGE,"E5.4.0")])]}),makeQuery(id+"F3.opExtrude","SWEPT_FACE",FACE,{"disambiguationData":[OSD([sQuery(id+"F2.wireOp",EDGE,"E5.5.0")])]})])],"derivedFrom":makeQuery(id+"F1.opExtrude","CAP_EDGE",EDGE,{"disambiguationData":[OSD([subQ0])],"isStart":true})});}
            var Q13;
            Q13=makeQuery(id+"F3.boolean.opBoolean","INTERSECT",EDGE,{"derivedFrom":[makeQuery(id+"F1.opExtrude","CAP_FACE",FACE,{"disambiguationData":[OSD([sQuery(id+"F0.wireOp",EDGE,"E0"),sQuery(id+"F0.wireOp",EDGE,"E1"),sQuery(id+"F0.wireOp",EDGE,"E2.0"),sQuery(id+"F0.wireOp",EDGE,"E2.1"),sQuery(id+"F0.wireOp",EDGE,"E2.2"),sQuery(id+"F0.wireOp",EDGE,"E2.3"),sQuery(id+"F0.wireOp",EDGE,"E2.4"),sQuery(id+"F0.wireOp",EDGE,"E2.5"),sQuery(id+"F0.wireOp",EDGE,"E3.1.0"),sQuery(id+"F0.wireOp",EDGE,"E3.1.1"),sQuery(id+"F0.wireOp",EDGE,"E3.1.2"),sQuery(id+"F0.wireOp",EDGE,"E3.1.3"),sQuery(id+"F0.wireOp",EDGE,"E3.1.4"),sQuery(id+"F0.wireOp",EDGE,"E3.1.5"),sQuery(id+"F0.wireOp",EDGE,"E3.2.0"),sQuery(id+"F0.wireOp",EDGE,"E3.2.1"),sQuery(id+"F0.wireOp",EDGE,"E3.2.2"),sQuery(id+"F0.wireOp",EDGE,"E3.2.3"),sQuery(id+"F0.wireOp",EDGE,"E3.2.4"),sQuery(id+"F0.wireOp",EDGE,"E3.2.5"),sQuery(id+"F0.wireOp",EDGE,"E3.3.0"),sQuery(id+"F0.wireOp",EDGE,"E3.3.1"),sQuery(id+"F0.wireOp",EDGE,"E3.3.2"),sQuery(id+"F0.wireOp",EDGE,"E3.3.3"),sQuery(id+"F0.wireOp",EDGE,"E3.3.4"),sQuery(id+"F0.wireOp",EDGE,"E3.3.5"),sQuery(id+"F0.wireOp",EDGE,"E3.4.0"),sQuery(id+"F0.wireOp",EDGE,"E3.4.1"),sQuery(id+"F0.wireOp",EDGE,"E3.4.2"),sQuery(id+"F0.wireOp",EDGE,"E3.4.3"),sQuery(id+"F0.wireOp",EDGE,"E3.4.4"),sQuery(id+"F0.wireOp",EDGE,"E3.4.5"),sQuery(id+"F0.wireOp",EDGE,"E3.5.0"),sQuery(id+"F0.wireOp",EDGE,"E3.5.1"),sQuery(id+"F0.wireOp",EDGE,"E3.5.2"),sQuery(id+"F0.wireOp",EDGE,"E3.5.3"),sQuery(id+"F0.wireOp",EDGE,"E3.5.4"),sQuery(id+"F0.wireOp",EDGE,"E3.5.5")])],"isStart":true}),makeQuery(id+"F3.opExtrude","SWEPT_FACE",FACE,{"disambiguationData":[OSD([sQuery(id+"F2.wireOp",EDGE,"E5.5.0")])]})]});
            var Q14;
            {var subQ0=sQuery(id+"F0.wireOp",EDGE,"E1");Q14=makeQuery(id+"F3.boolean.opBoolean","SPLIT",EDGE,{"disambiguationData":[TD([makeQuery(id+"F1.opExtrude","CAP_FACE",FACE,{"disambiguationData":[OSD([sQuery(id+"F0.wireOp",EDGE,"E0"),subQ0,sQuery(id+"F0.wireOp",EDGE,"E2.0"),sQuery(id+"F0.wireOp",EDGE,"E2.1"),sQuery(id+"F0.wireOp",EDGE,"E2.2"),sQuery(id+"F0.wireOp",EDGE,"E2.3"),sQuery(id+"F0.wireOp",EDGE,"E2.4"),sQuery(id+"F0.wireOp",EDGE,"E2.5"),sQuery(id+"F0.wireOp",EDGE,"E3.1.0"),sQuery(id+"F0.wireOp",EDGE,"E3.1.1"),sQuery(id+"F0.wireOp",EDGE,"E3.1.2"),sQuery(id+"F0.wireOp",EDGE,"E3.1.3"),sQuery(id+"F0.wireOp",EDGE,"E3.1.4"),sQuery(id+"F0.wireOp",EDGE,"E3.1.5"),sQuery(id+"F0.wireOp",EDGE,"E3.2.0"),sQuery(id+"F0.wireOp",EDGE,"E3.2.1"),sQuery(id+"F0.wireOp",EDGE,"E3.2.2"),sQuery(id+"F0.wireOp",EDGE,"E3.2.3"),sQuery(id+"F0.wireOp",EDGE,"E3.2.4"),sQuery(id+"F0.wireOp",EDGE,"E3.2.5"),sQuery(id+"F0.wireOp",EDGE,"E3.3.0"),sQuery(id+"F0.wireOp",EDGE,"E3.3.1"),sQuery(id+"F0.wireOp",EDGE,"E3.3.2"),sQuery(id+"F0.wireOp",EDGE,"E3.3.3"),sQuery(id+"F0.wireOp",EDGE,"E3.3.4"),sQuery(id+"F0.wireOp",EDGE,"E3.3.5"),sQuery(id+"F0.wireOp",EDGE,"E3.4.0"),sQuery(id+"F0.wireOp",EDGE,"E3.4.1"),sQuery(id+"F0.wireOp",EDGE,"E3.4.2"),sQuery(id+"F0.wireOp",EDGE,"E3.4.3"),sQuery(id+"F0.wireOp",EDGE,"E3.4.4"),sQuery(id+"F0.wireOp",EDGE,"E3.4.5"),sQuery(id+"F0.wireOp",EDGE,"E3.5.0"),sQuery(id+"F0.wireOp",EDGE,"E3.5.1"),sQuery(id+"F0.wireOp",EDGE,"E3.5.2"),sQuery(id+"F0.wireOp",EDGE,"E3.5.3"),sQuery(id+"F0.wireOp",EDGE,"E3.5.4"),sQuery(id+"F0.wireOp",EDGE,"E3.5.5")])],"isStart":true}),makeQuery(id+"F1.opExtrude","SWEPT_FACE",FACE,{"disambiguationData":[OSD([subQ0])]}),makeQuery(id+"F3.opExtrude","SWEPT_FACE",FACE,{"disambiguationData":[OSD([sQuery(id+"F2.wireOp",EDGE,"E4")])]}),makeQuery(id+"F3.opExtrude","SWEPT_FACE",FACE,{"disambiguationData":[OSD([sQuery(id+"F2.wireOp",EDGE,"E5.5.0")])]})])],"derivedFrom":makeQuery(id+"F1.opExtrude","CAP_EDGE",EDGE,{"disambiguationData":[OSD([subQ0])],"isStart":true})});}
            var Q15;
            Q15=makeQuery(id+"F3.boolean.opBoolean","INTERSECT",EDGE,{"derivedFrom":[makeQuery(id+"F1.opExtrude","CAP_FACE",FACE,{"disambiguationData":[OSD([sQuery(id+"F0.wireOp",EDGE,"E0"),sQuery(id+"F0.wireOp",EDGE,"E1"),sQuery(id+"F0.wireOp",EDGE,"E2.0"),sQuery(id+"F0.wireOp",EDGE,"E2.1"),sQuery(id+"F0.wireOp",EDGE,"E2.2"),sQuery(id+"F0.wireOp",EDGE,"E2.3"),sQuery(id+"F0.wireOp",EDGE,"E2.4"),sQuery(id+"F0.wireOp",EDGE,"E2.5"),sQuery(id+"F0.wireOp",EDGE,"E3.1.0"),sQuery(id+"F0.wireOp",EDGE,"E3.1.1"),sQuery(id+"F0.wireOp",EDGE,"E3.1.2"),sQuery(id+"F0.wireOp",EDGE,"E3.1.3"),sQuery(id+"F0.wireOp",EDGE,"E3.1.4"),sQuery(id+"F0.wireOp",EDGE,"E3.1.5"),sQuery(id+"F0.wireOp",EDGE,"E3.2.0"),sQuery(id+"F0.wireOp",EDGE,"E3.2.1"),sQuery(id+"F0.wireOp",EDGE,"E3.2.2"),sQuery(id+"F0.wireOp",EDGE,"E3.2.3"),sQuery(id+"F0.wireOp",EDGE,"E3.2.4"),sQuery(id+"F0.wireOp",EDGE,"E3.2.5"),sQuery(id+"F0.wireOp",EDGE,"E3.3.0"),sQuery(id+"F0.wireOp",EDGE,"E3.3.1"),sQuery(id+"F0.wireOp",EDGE,"E3.3.2"),sQuery(id+"F0.wireOp",EDGE,"E3.3.3"),sQuery(id+"F0.wireOp",EDGE,"E3.3.4"),sQuery(id+"F0.wireOp",EDGE,"E3.3.5"),sQuery(id+"F0.wireOp",EDGE,"E3.4.0"),sQuery(id+"F0.wireOp",EDGE,"E3.4.1"),sQuery(id+"F0.wireOp",EDGE,"E3.4.2"),sQuery(id+"F0.wireOp",EDGE,"E3.4.3"),sQuery(id+"F0.wireOp",EDGE,"E3.4.4"),sQuery(id+"F0.wireOp",EDGE,"E3.4.5"),sQuery(id+"F0.wireOp",EDGE,"E3.5.0"),sQuery(id+"F0.wireOp",EDGE,"E3.5.1"),sQuery(id+"F0.wireOp",EDGE,"E3.5.2"),sQuery(id+"F0.wireOp",EDGE,"E3.5.3"),sQuery(id+"F0.wireOp",EDGE,"E3.5.4"),sQuery(id+"F0.wireOp",EDGE,"E3.5.5")])],"isStart":true}),makeQuery(id+"F3.opExtrude","SWEPT_FACE",FACE,{"disambiguationData":[OSD([sQuery(id+"F2.wireOp",EDGE,"E4")])]})]});
            var Q16;
            {var subQ0=sQuery(id+"F0.wireOp",EDGE,"E1");Q16=makeQuery(id+"F3.boolean.opBoolean","SPLIT",EDGE,{"disambiguationData":[TD([makeQuery(id+"F1.opExtrude","CAP_FACE",FACE,{"disambiguationData":[OSD([sQuery(id+"F0.wireOp",EDGE,"E0"),subQ0,sQuery(id+"F0.wireOp",EDGE,"E2.0"),sQuery(id+"F0.wireOp",EDGE,"E2.1"),sQuery(id+"F0.wireOp",EDGE,"E2.2"),sQuery(id+"F0.wireOp",EDGE,"E2.3"),sQuery(id+"F0.wireOp",EDGE,"E2.4"),sQuery(id+"F0.wireOp",EDGE,"E2.5"),sQuery(id+"F0.wireOp",EDGE,"E3.1.0"),sQuery(id+"F0.wireOp",EDGE,"E3.1.1"),sQuery(id+"F0.wireOp",EDGE,"E3.1.2"),sQuery(id+"F0.wireOp",EDGE,"E3.1.3"),sQuery(id+"F0.wireOp",EDGE,"E3.1.4"),sQuery(id+"F0.wireOp",EDGE,"E3.1.5"),sQuery(id+"F0.wireOp",EDGE,"E3.2.0"),sQuery(id+"F0.wireOp",EDGE,"E3.2.1"),sQuery(id+"F0.wireOp",EDGE,"E3.2.2"),sQuery(id+"F0.wireOp",EDGE,"E3.2.3"),sQuery(id+"F0.wireOp",EDGE,"E3.2.4"),sQuery(id+"F0.wireOp",EDGE,"E3.2.5"),sQuery(id+"F0.wireOp",EDGE,"E3.3.0"),sQuery(id+"F0.wireOp",EDGE,"E3.3.1"),sQuery(id+"F0.wireOp",EDGE,"E3.3.2"),sQuery(id+"F0.wireOp",EDGE,"E3.3.3"),sQuery(id+"F0.wireOp",EDGE,"E3.3.4"),sQuery(id+"F0.wireOp",EDGE,"E3.3.5"),sQuery(id+"F0.wireOp",EDGE,"E3.4.0"),sQuery(id+"F0.wireOp",EDGE,"E3.4.1"),sQuery(id+"F0.wireOp",EDGE,"E3.4.2"),sQuery(id+"F0.wireOp",EDGE,"E3.4.3"),sQuery(id+"F0.wireOp",EDGE,"E3.4.4"),sQuery(id+"F0.wireOp",EDGE,"E3.4.5"),sQuery(id+"F0.wireOp",EDGE,"E3.5.0"),sQuery(id+"F0.wireOp",EDGE,"E3.5.1"),sQuery(id+"F0.wireOp",EDGE,"E3.5.2"),sQuery(id+"F0.wireOp",EDGE,"E3.5.3"),sQuery(id+"F0.wireOp",EDGE,"E3.5.4"),sQuery(id+"F0.wireOp",EDGE,"E3.5.5")])],"isStart":true}),makeQuery(id+"F1.opExtrude","SWEPT_FACE",FACE,{"disambiguationData":[OSD([subQ0])]}),makeQuery(id+"F3.opExtrude","SWEPT_FACE",FACE,{"disambiguationData":[OSD([sQuery(id+"F2.wireOp",EDGE,"E4")])]}),makeQuery(id+"F3.opExtrude","SWEPT_FACE",FACE,{"disambiguationData":[OSD([sQuery(id+"F2.wireOp",EDGE,"E5.1.0")])]})])],"derivedFrom":makeQuery(id+"F1.opExtrude","CAP_EDGE",EDGE,{"disambiguationData":[OSD([subQ0])],"isStart":true})});}
            var Q17;
            Q17=makeQuery(id+"F3.boolean.opBoolean","INTERSECT",EDGE,{"derivedFrom":[makeQuery(id+"F1.opExtrude","CAP_FACE",FACE,{"disambiguationData":[OSD([sQuery(id+"F0.wireOp",EDGE,"E0"),sQuery(id+"F0.wireOp",EDGE,"E1"),sQuery(id+"F0.wireOp",EDGE,"E2.0"),sQuery(id+"F0.wireOp",EDGE,"E2.1"),sQuery(id+"F0.wireOp",EDGE,"E2.2"),sQuery(id+"F0.wireOp",EDGE,"E2.3"),sQuery(id+"F0.wireOp",EDGE,"E2.4"),sQuery(id+"F0.wireOp",EDGE,"E2.5"),sQuery(id+"F0.wireOp",EDGE,"E3.1.0"),sQuery(id+"F0.wireOp",EDGE,"E3.1.1"),sQuery(id+"F0.wireOp",EDGE,"E3.1.2"),sQuery(id+"F0.wireOp",EDGE,"E3.1.3"),sQuery(id+"F0.wireOp",EDGE,"E3.1.4"),sQuery(id+"F0.wireOp",EDGE,"E3.1.5"),sQuery(id+"F0.wireOp",EDGE,"E3.2.0"),sQuery(id+"F0.wireOp",EDGE,"E3.2.1"),sQuery(id+"F0.wireOp",EDGE,"E3.2.2"),sQuery(id+"F0.wireOp",EDGE,"E3.2.3"),sQuery(id+"F0.wireOp",EDGE,"E3.2.4"),sQuery(id+"F0.wireOp",EDGE,"E3.2.5"),sQuery(id+"F0.wireOp",EDGE,"E3.3.0"),sQuery(id+"F0.wireOp",EDGE,"E3.3.1"),sQuery(id+"F0.wireOp",EDGE,"E3.3.2"),sQuery(id+"F0.wireOp",EDGE,"E3.3.3"),sQuery(id+"F0.wireOp",EDGE,"E3.3.4"),sQuery(id+"F0.wireOp",EDGE,"E3.3.5"),sQuery(id+"F0.wireOp",EDGE,"E3.4.0"),sQuery(id+"F0.wireOp",EDGE,"E3.4.1"),sQuery(id+"F0.wireOp",EDGE,"E3.4.2"),sQuery(id+"F0.wireOp",EDGE,"E3.4.3"),sQuery(id+"F0.wireOp",EDGE,"E3.4.4"),sQuery(id+"F0.wireOp",EDGE,"E3.4.5"),sQuery(id+"F0.wireOp",EDGE,"E3.5.0"),sQuery(id+"F0.wireOp",EDGE,"E3.5.1"),sQuery(id+"F0.wireOp",EDGE,"E3.5.2"),sQuery(id+"F0.wireOp",EDGE,"E3.5.3"),sQuery(id+"F0.wireOp",EDGE,"E3.5.4"),sQuery(id+"F0.wireOp",EDGE,"E3.5.5")])],"isStart":true}),makeQuery(id+"F3.opExtrude","SWEPT_FACE",FACE,{"disambiguationData":[OSD([sQuery(id+"F2.wireOp",EDGE,"E5.1.0")])]})]});
            var Q18;
            {var subQ0=sQuery(id+"F0.wireOp",EDGE,"E1");Q18=makeQuery(id+"F3.boolean.opBoolean","SPLIT",EDGE,{"disambiguationData":[TD([makeQuery(id+"F1.opExtrude","CAP_FACE",FACE,{"disambiguationData":[OSD([sQuery(id+"F0.wireOp",EDGE,"E0"),subQ0,sQuery(id+"F0.wireOp",EDGE,"E2.0"),sQuery(id+"F0.wireOp",EDGE,"E2.1"),sQuery(id+"F0.wireOp",EDGE,"E2.2"),sQuery(id+"F0.wireOp",EDGE,"E2.3"),sQuery(id+"F0.wireOp",EDGE,"E2.4"),sQuery(id+"F0.wireOp",EDGE,"E2.5"),sQuery(id+"F0.wireOp",EDGE,"E3.1.0"),sQuery(id+"F0.wireOp",EDGE,"E3.1.1"),sQuery(id+"F0.wireOp",EDGE,"E3.1.2"),sQuery(id+"F0.wireOp",EDGE,"E3.1.3"),sQuery(id+"F0.wireOp",EDGE,"E3.1.4"),sQuery(id+"F0.wireOp",EDGE,"E3.1.5"),sQuery(id+"F0.wireOp",EDGE,"E3.2.0"),sQuery(id+"F0.wireOp",EDGE,"E3.2.1"),sQuery(id+"F0.wireOp",EDGE,"E3.2.2"),sQuery(id+"F0.wireOp",EDGE,"E3.2.3"),sQuery(id+"F0.wireOp",EDGE,"E3.2.4"),sQuery(id+"F0.wireOp",EDGE,"E3.2.5"),sQuery(id+"F0.wireOp",EDGE,"E3.3.0"),sQuery(id+"F0.wireOp",EDGE,"E3.3.1"),sQuery(id+"F0.wireOp",EDGE,"E3.3.2"),sQuery(id+"F0.wireOp",EDGE,"E3.3.3"),sQuery(id+"F0.wireOp",EDGE,"E3.3.4"),sQuery(id+"F0.wireOp",EDGE,"E3.3.5"),sQuery(id+"F0.wireOp",EDGE,"E3.4.0"),sQuery(id+"F0.wireOp",EDGE,"E3.4.1"),sQuery(id+"F0.wireOp",EDGE,"E3.4.2"),sQuery(id+"F0.wireOp",EDGE,"E3.4.3"),sQuery(id+"F0.wireOp",EDGE,"E3.4.4"),sQuery(id+"F0.wireOp",EDGE,"E3.4.5"),sQuery(id+"F0.wireOp",EDGE,"E3.5.0"),sQuery(id+"F0.wireOp",EDGE,"E3.5.1"),sQuery(id+"F0.wireOp",EDGE,"E3.5.2"),sQuery(id+"F0.wireOp",EDGE,"E3.5.3"),sQuery(id+"F0.wireOp",EDGE,"E3.5.4"),sQuery(id+"F0.wireOp",EDGE,"E3.5.5")])],"isStart":true}),makeQuery(id+"F1.opExtrude","SWEPT_FACE",FACE,{"disambiguationData":[OSD([subQ0])]}),makeQuery(id+"F3.opExtrude","SWEPT_FACE",FACE,{"disambiguationData":[OSD([sQuery(id+"F2.wireOp",EDGE,"E5.1.0")])]}),makeQuery(id+"F3.opExtrude","SWEPT_FACE",FACE,{"disambiguationData":[OSD([sQuery(id+"F2.wireOp",EDGE,"E5.2.0")])]})])],"derivedFrom":makeQuery(id+"F1.opExtrude","CAP_EDGE",EDGE,{"disambiguationData":[OSD([subQ0])],"isStart":true})});}
            var Q19;
            Q19=makeQuery(id+"F3.boolean.opBoolean","INTERSECT",EDGE,{"derivedFrom":[makeQuery(id+"F1.opExtrude","CAP_FACE",FACE,{"disambiguationData":[OSD([sQuery(id+"F0.wireOp",EDGE,"E0"),sQuery(id+"F0.wireOp",EDGE,"E1"),sQuery(id+"F0.wireOp",EDGE,"E2.0"),sQuery(id+"F0.wireOp",EDGE,"E2.1"),sQuery(id+"F0.wireOp",EDGE,"E2.2"),sQuery(id+"F0.wireOp",EDGE,"E2.3"),sQuery(id+"F0.wireOp",EDGE,"E2.4"),sQuery(id+"F0.wireOp",EDGE,"E2.5"),sQuery(id+"F0.wireOp",EDGE,"E3.1.0"),sQuery(id+"F0.wireOp",EDGE,"E3.1.1"),sQuery(id+"F0.wireOp",EDGE,"E3.1.2"),sQuery(id+"F0.wireOp",EDGE,"E3.1.3"),sQuery(id+"F0.wireOp",EDGE,"E3.1.4"),sQuery(id+"F0.wireOp",EDGE,"E3.1.5"),sQuery(id+"F0.wireOp",EDGE,"E3.2.0"),sQuery(id+"F0.wireOp",EDGE,"E3.2.1"),sQuery(id+"F0.wireOp",EDGE,"E3.2.2"),sQuery(id+"F0.wireOp",EDGE,"E3.2.3"),sQuery(id+"F0.wireOp",EDGE,"E3.2.4"),sQuery(id+"F0.wireOp",EDGE,"E3.2.5"),sQuery(id+"F0.wireOp",EDGE,"E3.3.0"),sQuery(id+"F0.wireOp",EDGE,"E3.3.1"),sQuery(id+"F0.wireOp",EDGE,"E3.3.2"),sQuery(id+"F0.wireOp",EDGE,"E3.3.3"),sQuery(id+"F0.wireOp",EDGE,"E3.3.4"),sQuery(id+"F0.wireOp",EDGE,"E3.3.5"),sQuery(id+"F0.wireOp",EDGE,"E3.4.0"),sQuery(id+"F0.wireOp",EDGE,"E3.4.1"),sQuery(id+"F0.wireOp",EDGE,"E3.4.2"),sQuery(id+"F0.wireOp",EDGE,"E3.4.3"),sQuery(id+"F0.wireOp",EDGE,"E3.4.4"),sQuery(id+"F0.wireOp",EDGE,"E3.4.5"),sQuery(id+"F0.wireOp",EDGE,"E3.5.0"),sQuery(id+"F0.wireOp",EDGE,"E3.5.1"),sQuery(id+"F0.wireOp",EDGE,"E3.5.2"),sQuery(id+"F0.wireOp",EDGE,"E3.5.3"),sQuery(id+"F0.wireOp",EDGE,"E3.5.4"),sQuery(id+"F0.wireOp",EDGE,"E3.5.5")])],"isStart":true}),makeQuery(id+"F3.opExtrude","SWEPT_FACE",FACE,{"disambiguationData":[OSD([sQuery(id+"F2.wireOp",EDGE,"E5.2.0")])]})]});
            var Q20;
            {var subQ0=sQuery(id+"F0.wireOp",EDGE,"E1");Q20=makeQuery(id+"F3.boolean.opBoolean","SPLIT",EDGE,{"disambiguationData":[TD([makeQuery(id+"F1.opExtrude","CAP_FACE",FACE,{"disambiguationData":[OSD([sQuery(id+"F0.wireOp",EDGE,"E0"),subQ0,sQuery(id+"F0.wireOp",EDGE,"E2.0"),sQuery(id+"F0.wireOp",EDGE,"E2.1"),sQuery(id+"F0.wireOp",EDGE,"E2.2"),sQuery(id+"F0.wireOp",EDGE,"E2.3"),sQuery(id+"F0.wireOp",EDGE,"E2.4"),sQuery(id+"F0.wireOp",EDGE,"E2.5"),sQuery(id+"F0.wireOp",EDGE,"E3.1.0"),sQuery(id+"F0.wireOp",EDGE,"E3.1.1"),sQuery(id+"F0.wireOp",EDGE,"E3.1.2"),sQuery(id+"F0.wireOp",EDGE,"E3.1.3"),sQuery(id+"F0.wireOp",EDGE,"E3.1.4"),sQuery(id+"F0.wireOp",EDGE,"E3.1.5"),sQuery(id+"F0.wireOp",EDGE,"E3.2.0"),sQuery(id+"F0.wireOp",EDGE,"E3.2.1"),sQuery(id+"F0.wireOp",EDGE,"E3.2.2"),sQuery(id+"F0.wireOp",EDGE,"E3.2.3"),sQuery(id+"F0.wireOp",EDGE,"E3.2.4"),sQuery(id+"F0.wireOp",EDGE,"E3.2.5"),sQuery(id+"F0.wireOp",EDGE,"E3.3.0"),sQuery(id+"F0.wireOp",EDGE,"E3.3.1"),sQuery(id+"F0.wireOp",EDGE,"E3.3.2"),sQuery(id+"F0.wireOp",EDGE,"E3.3.3"),sQuery(id+"F0.wireOp",EDGE,"E3.3.4"),sQuery(id+"F0.wireOp",EDGE,"E3.3.5"),sQuery(id+"F0.wireOp",EDGE,"E3.4.0"),sQuery(id+"F0.wireOp",EDGE,"E3.4.1"),sQuery(id+"F0.wireOp",EDGE,"E3.4.2"),sQuery(id+"F0.wireOp",EDGE,"E3.4.3"),sQuery(id+"F0.wireOp",EDGE,"E3.4.4"),sQuery(id+"F0.wireOp",EDGE,"E3.4.5"),sQuery(id+"F0.wireOp",EDGE,"E3.5.0"),sQuery(id+"F0.wireOp",EDGE,"E3.5.1"),sQuery(id+"F0.wireOp",EDGE,"E3.5.2"),sQuery(id+"F0.wireOp",EDGE,"E3.5.3"),sQuery(id+"F0.wireOp",EDGE,"E3.5.4"),sQuery(id+"F0.wireOp",EDGE,"E3.5.5")])],"isStart":true}),makeQuery(id+"F1.opExtrude","SWEPT_FACE",FACE,{"disambiguationData":[OSD([subQ0])]}),makeQuery(id+"F3.opExtrude","SWEPT_FACE",FACE,{"disambiguationData":[OSD([sQuery(id+"F2.wireOp",EDGE,"E5.2.0")])]}),makeQuery(id+"F3.opExtrude","SWEPT_FACE",FACE,{"disambiguationData":[OSD([sQuery(id+"F2.wireOp",EDGE,"E5.3.0")])]})])],"derivedFrom":makeQuery(id+"F1.opExtrude","CAP_EDGE",EDGE,{"disambiguationData":[OSD([subQ0])],"isStart":true})});}
            var Q21;
            Q21=makeQuery(id+"F3.boolean.opBoolean","INTERSECT",EDGE,{"derivedFrom":[makeQuery(id+"F1.opExtrude","CAP_FACE",FACE,{"disambiguationData":[OSD([sQuery(id+"F0.wireOp",EDGE,"E0"),sQuery(id+"F0.wireOp",EDGE,"E1"),sQuery(id+"F0.wireOp",EDGE,"E2.0"),sQuery(id+"F0.wireOp",EDGE,"E2.1"),sQuery(id+"F0.wireOp",EDGE,"E2.2"),sQuery(id+"F0.wireOp",EDGE,"E2.3"),sQuery(id+"F0.wireOp",EDGE,"E2.4"),sQuery(id+"F0.wireOp",EDGE,"E2.5"),sQuery(id+"F0.wireOp",EDGE,"E3.1.0"),sQuery(id+"F0.wireOp",EDGE,"E3.1.1"),sQuery(id+"F0.wireOp",EDGE,"E3.1.2"),sQuery(id+"F0.wireOp",EDGE,"E3.1.3"),sQuery(id+"F0.wireOp",EDGE,"E3.1.4"),sQuery(id+"F0.wireOp",EDGE,"E3.1.5"),sQuery(id+"F0.wireOp",EDGE,"E3.2.0"),sQuery(id+"F0.wireOp",EDGE,"E3.2.1"),sQuery(id+"F0.wireOp",EDGE,"E3.2.2"),sQuery(id+"F0.wireOp",EDGE,"E3.2.3"),sQuery(id+"F0.wireOp",EDGE,"E3.2.4"),sQuery(id+"F0.wireOp",EDGE,"E3.2.5"),sQuery(id+"F0.wireOp",EDGE,"E3.3.0"),sQuery(id+"F0.wireOp",EDGE,"E3.3.1"),sQuery(id+"F0.wireOp",EDGE,"E3.3.2"),sQuery(id+"F0.wireOp",EDGE,"E3.3.3"),sQuery(id+"F0.wireOp",EDGE,"E3.3.4"),sQuery(id+"F0.wireOp",EDGE,"E3.3.5"),sQuery(id+"F0.wireOp",EDGE,"E3.4.0"),sQuery(id+"F0.wireOp",EDGE,"E3.4.1"),sQuery(id+"F0.wireOp",EDGE,"E3.4.2"),sQuery(id+"F0.wireOp",EDGE,"E3.4.3"),sQuery(id+"F0.wireOp",EDGE,"E3.4.4"),sQuery(id+"F0.wireOp",EDGE,"E3.4.5"),sQuery(id+"F0.wireOp",EDGE,"E3.5.0"),sQuery(id+"F0.wireOp",EDGE,"E3.5.1"),sQuery(id+"F0.wireOp",EDGE,"E3.5.2"),sQuery(id+"F0.wireOp",EDGE,"E3.5.3"),sQuery(id+"F0.wireOp",EDGE,"E3.5.4"),sQuery(id+"F0.wireOp",EDGE,"E3.5.5")])],"isStart":true}),makeQuery(id+"F3.opExtrude","SWEPT_FACE",FACE,{"disambiguationData":[OSD([sQuery(id+"F2.wireOp",EDGE,"E5.3.0")])]})]});
            var Q22;
            {var subQ0=sQuery(id+"F0.wireOp",EDGE,"E1");Q22=makeQuery(id+"F3.boolean.opBoolean","SPLIT",EDGE,{"disambiguationData":[TD([makeQuery(id+"F1.opExtrude","CAP_FACE",FACE,{"disambiguationData":[OSD([sQuery(id+"F0.wireOp",EDGE,"E0"),subQ0,sQuery(id+"F0.wireOp",EDGE,"E2.0"),sQuery(id+"F0.wireOp",EDGE,"E2.1"),sQuery(id+"F0.wireOp",EDGE,"E2.2"),sQuery(id+"F0.wireOp",EDGE,"E2.3"),sQuery(id+"F0.wireOp",EDGE,"E2.4"),sQuery(id+"F0.wireOp",EDGE,"E2.5"),sQuery(id+"F0.wireOp",EDGE,"E3.1.0"),sQuery(id+"F0.wireOp",EDGE,"E3.1.1"),sQuery(id+"F0.wireOp",EDGE,"E3.1.2"),sQuery(id+"F0.wireOp",EDGE,"E3.1.3"),sQuery(id+"F0.wireOp",EDGE,"E3.1.4"),sQuery(id+"F0.wireOp",EDGE,"E3.1.5"),sQuery(id+"F0.wireOp",EDGE,"E3.2.0"),sQuery(id+"F0.wireOp",EDGE,"E3.2.1"),sQuery(id+"F0.wireOp",EDGE,"E3.2.2"),sQuery(id+"F0.wireOp",EDGE,"E3.2.3"),sQuery(id+"F0.wireOp",EDGE,"E3.2.4"),sQuery(id+"F0.wireOp",EDGE,"E3.2.5"),sQuery(id+"F0.wireOp",EDGE,"E3.3.0"),sQuery(id+"F0.wireOp",EDGE,"E3.3.1"),sQuery(id+"F0.wireOp",EDGE,"E3.3.2"),sQuery(id+"F0.wireOp",EDGE,"E3.3.3"),sQuery(id+"F0.wireOp",EDGE,"E3.3.4"),sQuery(id+"F0.wireOp",EDGE,"E3.3.5"),sQuery(id+"F0.wireOp",EDGE,"E3.4.0"),sQuery(id+"F0.wireOp",EDGE,"E3.4.1"),sQuery(id+"F0.wireOp",EDGE,"E3.4.2"),sQuery(id+"F0.wireOp",EDGE,"E3.4.3"),sQuery(id+"F0.wireOp",EDGE,"E3.4.4"),sQuery(id+"F0.wireOp",EDGE,"E3.4.5"),sQuery(id+"F0.wireOp",EDGE,"E3.5.0"),sQuery(id+"F0.wireOp",EDGE,"E3.5.1"),sQuery(id+"F0.wireOp",EDGE,"E3.5.2"),sQuery(id+"F0.wireOp",EDGE,"E3.5.3"),sQuery(id+"F0.wireOp",EDGE,"E3.5.4"),sQuery(id+"F0.wireOp",EDGE,"E3.5.5")])],"isStart":true}),makeQuery(id+"F1.opExtrude","SWEPT_FACE",FACE,{"disambiguationData":[OSD([subQ0])]}),makeQuery(id+"F3.opExtrude","SWEPT_FACE",FACE,{"disambiguationData":[OSD([sQuery(id+"F2.wireOp",EDGE,"E5.3.0")])]}),makeQuery(id+"F3.opExtrude","SWEPT_FACE",FACE,{"disambiguationData":[OSD([sQuery(id+"F2.wireOp",EDGE,"E5.4.0")])]})])],"derivedFrom":makeQuery(id+"F1.opExtrude","CAP_EDGE",EDGE,{"disambiguationData":[OSD([subQ0])],"isStart":true})});}
            var Q23;
            Q23=makeQuery(id+"F3.boolean.opBoolean","INTERSECT",EDGE,{"disambiguationData":[OD(1.0)],"derivedFrom":[makeQuery(id+"F1.opExtrude","SWEPT_FACE",FACE,{"disambiguationData":[OSD([sQuery(id+"F0.wireOp",EDGE,"E1")])]}),makeQuery(id+"F3.opExtrude","SWEPT_FACE",FACE,{"disambiguationData":[OSD([sQuery(id+"F2.wireOp",EDGE,"E4")])]})]});
            var Q24;
            Q24=makeQuery(id+"F3.boolean.opBoolean","INTERSECT",EDGE,{"disambiguationData":[OD(0.0)],"derivedFrom":[makeQuery(id+"F1.opExtrude","SWEPT_FACE",FACE,{"disambiguationData":[OSD([sQuery(id+"F0.wireOp",EDGE,"E1")])]}),makeQuery(id+"F3.opExtrude","SWEPT_FACE",FACE,{"disambiguationData":[OSD([sQuery(id+"F2.wireOp",EDGE,"E4")])]})]});
            var Q25;
            Q25=makeQuery(id+"F3.boolean.opBoolean","INTERSECT",EDGE,{"disambiguationData":[OD(0.0)],"derivedFrom":[makeQuery(id+"F1.opExtrude","SWEPT_FACE",FACE,{"disambiguationData":[OSD([sQuery(id+"F0.wireOp",EDGE,"E1")])]}),makeQuery(id+"F3.opExtrude","SWEPT_FACE",FACE,{"disambiguationData":[OSD([sQuery(id+"F2.wireOp",EDGE,"E5.1.0")])]})]});
            var Q26;
            {var subQ0=sQuery(id+"F0.wireOp",EDGE,"E3.5.5");var subQ1=sQuery(id+"F0.wireOp",EDGE,"E3.5.4");var subQ2=sQuery(id+"F0.wireOp",EDGE,"E3.5.3");var subQ3=sQuery(id+"F0.wireOp",EDGE,"E3.5.2");var subQ4=sQuery(id+"F0.wireOp",EDGE,"E3.5.1");var subQ5=sQuery(id+"F0.wireOp",EDGE,"E3.5.0");var subQ6=sQuery(id+"F0.wireOp",EDGE,"E3.4.5");var subQ7=sQuery(id+"F0.wireOp",EDGE,"E3.4.4");var subQ8=sQuery(id+"F0.wireOp",EDGE,"E3.4.3");var subQ9=sQuery(id+"F0.wireOp",EDGE,"E3.4.2");var subQ10=sQuery(id+"F0.wireOp",EDGE,"E3.4.1");var subQ11=sQuery(id+"F0.wireOp",EDGE,"E3.4.0");var subQ12=sQuery(id+"F0.wireOp",EDGE,"E3.3.5");var subQ13=sQuery(id+"F0.wireOp",EDGE,"E3.3.4");var subQ14=sQuery(id+"F0.wireOp",EDGE,"E3.3.3");var subQ15=sQuery(id+"F0.wireOp",EDGE,"E3.3.2");var subQ16=sQuery(id+"F0.wireOp",EDGE,"E3.3.1");var subQ17=sQuery(id+"F0.wireOp",EDGE,"E3.3.0");var subQ18=sQuery(id+"F0.wireOp",EDGE,"E3.2.5");var subQ19=sQuery(id+"F0.wireOp",EDGE,"E3.2.4");var subQ20=sQuery(id+"F0.wireOp",EDGE,"E3.2.3");var subQ21=sQuery(id+"F0.wireOp",EDGE,"E3.2.2");var subQ22=sQuery(id+"F0.wireOp",EDGE,"E3.2.1");var subQ23=sQuery(id+"F0.wireOp",EDGE,"E3.2.0");var subQ24=sQuery(id+"F0.wireOp",EDGE,"E3.1.5");var subQ25=sQuery(id+"F0.wireOp",EDGE,"E3.1.4");var subQ26=sQuery(id+"F0.wireOp",EDGE,"E3.1.3");var subQ27=sQuery(id+"F0.wireOp",EDGE,"E3.1.2");var subQ28=sQuery(id+"F0.wireOp",EDGE,"E3.1.1");var subQ29=sQuery(id+"F0.wireOp",EDGE,"E3.1.0");var subQ30=sQuery(id+"F0.wireOp",EDGE,"E2.5");var subQ31=sQuery(id+"F0.wireOp",EDGE,"E2.4");var subQ32=sQuery(id+"F0.wireOp",EDGE,"E2.3");var subQ33=sQuery(id+"F0.wireOp",EDGE,"E2.2");var subQ34=sQuery(id+"F0.wireOp",EDGE,"E2.1");var subQ35=sQuery(id+"F0.wireOp",EDGE,"E2.0");var subQ36=sQuery(id+"F0.wireOp",EDGE,"E1");var subQ37=sQuery(id+"F0.wireOp",EDGE,"E0");Q26=makeQuery(id+"F3.boolean.opBoolean","SPLIT",FACE,{"disambiguationData":[TD([makeQuery(id+"F1.opExtrude","CAP_FACE",FACE,{"disambiguationData":[OSD([subQ37,subQ36,subQ35,subQ34,subQ33,subQ32,subQ31,subQ30,subQ29,subQ28,subQ27,subQ26,subQ25,subQ24,subQ23,subQ22,subQ21,subQ20,subQ19,subQ18,subQ17,subQ16,subQ15,subQ14,subQ13,subQ12,subQ11,subQ10,subQ9,subQ8,subQ7,subQ6,subQ5,subQ4,subQ3,subQ2,subQ1,subQ0])],"isStart":true}),makeQuery(id+"F1.opExtrude","CAP_FACE",FACE,{"disambiguationData":[OSD([subQ37,subQ36,subQ35,subQ34,subQ33,subQ32,subQ31,subQ30,subQ29,subQ28,subQ27,subQ26,subQ25,subQ24,subQ23,subQ22,subQ21,subQ20,subQ19,subQ18,subQ17,subQ16,subQ15,subQ14,subQ13,subQ12,subQ11,subQ10,subQ9,subQ8,subQ7,subQ6,subQ5,subQ4,subQ3,subQ2,subQ1,subQ0])],"isStart":false}),makeQuery(id+"F3.opExtrude","SWEPT_FACE",FACE,{"disambiguationData":[OSD([sQuery(id+"F2.wireOp",EDGE,"E5.1.0")])]}),makeQuery(id+"F3.opExtrude","SWEPT_FACE",FACE,{"disambiguationData":[OSD([sQuery(id+"F2.wireOp",EDGE,"E5.2.0")])]})])],"derivedFrom":makeQuery(id+"F1.opExtrude","SWEPT_FACE",FACE,{"disambiguationData":[OSD([subQ36])]})});}
            var Q27;
            Q27=makeQuery(id+"F3.boolean.opBoolean","INTERSECT",EDGE,{"disambiguationData":[OD(1.0)],"derivedFrom":[makeQuery(id+"F1.opExtrude","SWEPT_FACE",FACE,{"disambiguationData":[OSD([sQuery(id+"F0.wireOp",EDGE,"E1")])]}),makeQuery(id+"F3.opExtrude","SWEPT_FACE",FACE,{"disambiguationData":[OSD([sQuery(id+"F2.wireOp",EDGE,"E5.2.0")])]})]});
            var Q28;
            Q28=makeQuery(id+"F3.boolean.opBoolean","INTERSECT",EDGE,{"disambiguationData":[OD(0.0)],"derivedFrom":[makeQuery(id+"F1.opExtrude","SWEPT_FACE",FACE,{"disambiguationData":[OSD([sQuery(id+"F0.wireOp",EDGE,"E1")])]}),makeQuery(id+"F3.opExtrude","SWEPT_FACE",FACE,{"disambiguationData":[OSD([sQuery(id+"F2.wireOp",EDGE,"E5.2.0")])]})]});
            var Q29;
            Q29=makeQuery(id+"F3.boolean.opBoolean","INTERSECT",EDGE,{"disambiguationData":[OD(1.0)],"derivedFrom":[makeQuery(id+"F1.opExtrude","SWEPT_FACE",FACE,{"disambiguationData":[OSD([sQuery(id+"F0.wireOp",EDGE,"E1")])]}),makeQuery(id+"F3.opExtrude","SWEPT_FACE",FACE,{"disambiguationData":[OSD([sQuery(id+"F2.wireOp",EDGE,"E5.3.0")])]})]});
            var Q30;
            Q30=makeQuery(id+"F3.boolean.opBoolean","COPY",FACE,{"derivedFrom":makeQuery(id+"F3.opExtrude","SWEPT_FACE",FACE,{"disambiguationData":[OSD([sQuery(id+"F2.wireOp",EDGE,"E5.3.0")])]})});
            var Q31;
            Q31=makeQuery(id+"F3.boolean.opBoolean","INTERSECT",EDGE,{"disambiguationData":[OD(0.0)],"derivedFrom":[makeQuery(id+"F1.opExtrude","SWEPT_FACE",FACE,{"disambiguationData":[OSD([sQuery(id+"F0.wireOp",EDGE,"E1")])]}),makeQuery(id+"F3.opExtrude","SWEPT_FACE",FACE,{"disambiguationData":[OSD([sQuery(id+"F2.wireOp",EDGE,"E5.4.0")])]})]});
            var Q32;
            Q32=makeQuery(id+"F3.boolean.opBoolean","INTERSECT",EDGE,{"disambiguationData":[OD(1.0)],"derivedFrom":[makeQuery(id+"F1.opExtrude","SWEPT_FACE",FACE,{"disambiguationData":[OSD([sQuery(id+"F0.wireOp",EDGE,"E1")])]}),makeQuery(id+"F3.opExtrude","SWEPT_FACE",FACE,{"disambiguationData":[OSD([sQuery(id+"F2.wireOp",EDGE,"E5.4.0")])]})]});
            var Q33;
            Q33=makeQuery(id+"F3.boolean.opBoolean","INTERSECT",EDGE,{"disambiguationData":[OD(1.0)],"derivedFrom":[makeQuery(id+"F1.opExtrude","SWEPT_FACE",FACE,{"disambiguationData":[OSD([sQuery(id+"F0.wireOp",EDGE,"E1")])]}),makeQuery(id+"F3.opExtrude","SWEPT_FACE",FACE,{"disambiguationData":[OSD([sQuery(id+"F2.wireOp",EDGE,"E5.5.0")])]})]});
            var Q34;
            Q34=makeQuery(id+"F3.boolean.opBoolean","INTERSECT",EDGE,{"disambiguationData":[OD(0.0)],"derivedFrom":[makeQuery(id+"F1.opExtrude","SWEPT_FACE",FACE,{"disambiguationData":[OSD([sQuery(id+"F0.wireOp",EDGE,"E1")])]}),makeQuery(id+"F3.opExtrude","SWEPT_FACE",FACE,{"disambiguationData":[OSD([sQuery(id+"F2.wireOp",EDGE,"E5.5.0")])]})]});
            var Q35;
            Q35=makeQuery(id+"F1.opExtrude","CAP_EDGE",EDGE,{"disambiguationData":[OSD([sQuery(id+"F0.wireOp",EDGE,"E0")])],"isStart":false});
            var Q36;
            Q36=makeQuery(id+"F1.opExtrude","CAP_EDGE",EDGE,{"disambiguationData":[OSD([sQuery(id+"F0.wireOp",EDGE,"E0")])],"isStart":true});
            fillet(context, id + "F4", {"entities" : qUnion([Q0, Q1, Q2, Q3, Q4, Q5, Q6, Q7, Q8, Q9, Q10, Q11, Q12, Q13, Q14, Q15, Q16, Q17, Q18, Q19, Q20, Q21, Q22, Q23, Q24, Q25, Q26, Q27, Q28, Q29, Q30, Q31, Q32, Q33, Q34, Q35, Q36]), "radius" : 1.5 * mm, "tangentPropagation" : true, "allowEdgeOverflow" : false});
        }
    });
